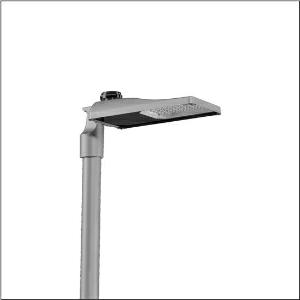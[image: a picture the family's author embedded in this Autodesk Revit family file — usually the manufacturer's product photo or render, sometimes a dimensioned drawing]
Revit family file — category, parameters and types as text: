
# Revit family: streetlight_sl_31_mini___st1_0a_5xh6d3bn08ja_1c18
name_source: partatom
category: Lighting Fixtures
units: mm (PartAtom-declared; Revit-internal decimal feet)

## family parameters
Cut with Voids When Loaded = No
Host = Face
Light Source = No
Part Type = Normal
Room Calculation Point = No
Round Connector Dimension = Use Diameter
Shared = No

## types (1)
- --- (1 x LED, 12140 lm, 81.1 W, 3000K)
    Apparent Load = 81 VA
    CIE Flux Codes = 40 73 97 100 100
    Color Rendering = 70
    Color Temperature = 3000K
    Default Elevation = 1800 mm
    Description = Streetlight SL 31 mini, mast luminaire, primary light control with lens, of PMMA, primary optical cover: cover, of toughened safety glass, transparent, light distribution: ST1.0a, light emission: direct distribution, primary light characteristic: asymmetric, installation type: post-top, side-entry, LED, High Power LED, rated luminous flux: 12.140lm, luminous efficacy: 150lm/W, light colour: 730, colour temperature: 3000K, control: presetting dimming linear, flexible luminous flux parameterisation, time-dependent luminous flux control, constant luminous flux control, intelligent temperature release in ECG and LED module, overheat protection, with cable H07RN-F 3x 1.5mm², mains connection: 220..240V, AC, 50/60Hz, connection cable pre-assembled, cable length: 10,5m, start of lifetime: 81W, end of service life: 88W, reduction: 36W, luminaire housing, of diecast aluminium, powder-coated, Siteco® metallic grey (DB 702S), corrosivity category C5 high according to DIN EN ISO 12944, no sealing on luminaire upper side, inclination: -15°..+20° (post-top) | -20°..+20° (side-entry), adjustable in 5° steps, mast flange (76/60mm) included as standard, multi-level sealing system, sealing non-destructively replaceable, protection rating (complete): IP66, insulation class (complete): insulation class I (protective earthing), certification: CE, ENEC, ENEC+, VDE, UKCA, impact resistance: IK09, permissible operating ambient temperature for outdoor applications: -40..+50°C, standard-compliant lighting for roads and squares, packaging unit: 1 piece

Light Distribution: ST1.0a
    Height = 76 mm
    Lamp = 1 x LED
    Lamp Light Flux = 12140 lm
    Lamp Power = 81.1 W
    Lamp count = 1
    Length = 547 mm
    Luminous efficacy = 150 lm/W
    Manufacturer = Siteco
    ModVariant = No
    Model = 5XH6D3BN08JA
    Number of Poles = 1
    OnlyDefault = Yes
    Power Factor = 1
    Product Name = Streetlight SL 31 mini | ST1.0a
    Product group = mast luminaire | pylon top
    ProductGroupID = 6100
    Protection Class = Protection class I
    Protection Degree = IP 66
    RLX_Detail_Level = 1
    RLX_Emergency_Light_Flux = 0 lm
    RLX_Emergency_Type = 0
    RLX_Emergency_Type_DB = No
    RlxData = <blob elided: 40553 chars, md5=33dd3d0a>
    Socket = socket
    Standby Power = 0 W
    System Light Flux = 12140 lm
    System Power = 81 W
    Type Comments = factory setting: luminous flux: 100 % | dim-lin: 254 | 860 mA
    Type Image = l_1300322.jpg
    URL = http://relux.com
    VarID = @adj_007695
    Voltage = 0 V
    Weight = 0.00 kg
    Width = 265 mm

## geometry (parser evidence)
native form markers: Blend x4, Sweep x9
no freeform markers — native parametric forms only
